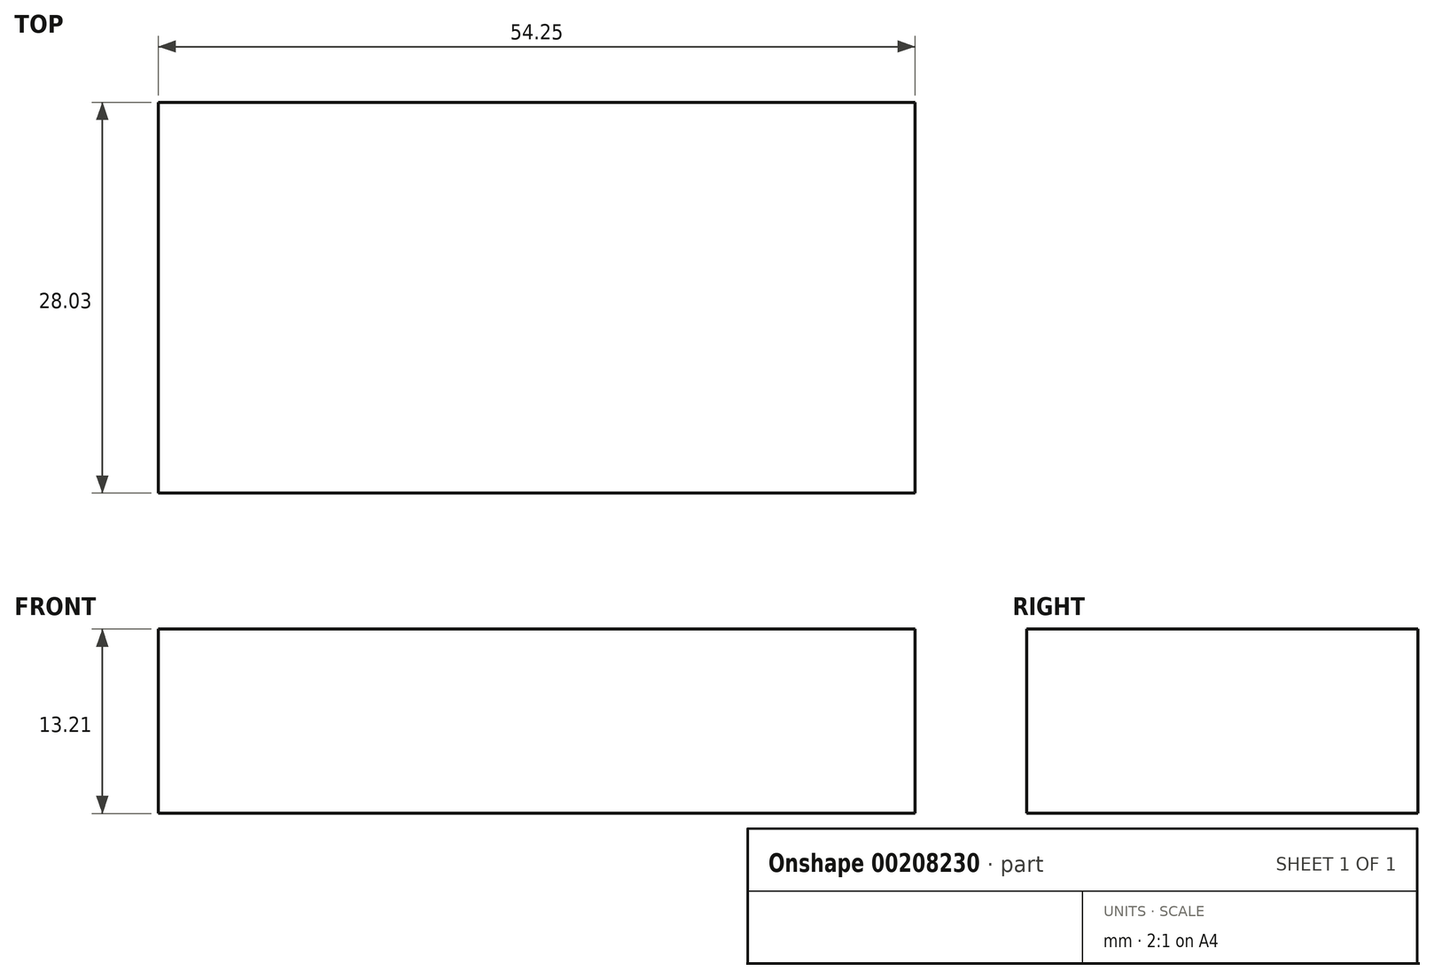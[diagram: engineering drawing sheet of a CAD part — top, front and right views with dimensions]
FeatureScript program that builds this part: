
annotation { "Feature Type Name" : "Feature", "Feature Type Description" : "" }
export const myFeature = defineFeature(function(context is Context, id is Id, definition is map)
    precondition{}
    {
        {
            var Q0;
            Q0=qCreatedBy(makeId("Top.planeOp"),FACE);
            var sketch = newSketch(context, id + "F0", { "sketchPlane" : qUnion([Q0])});
            skLineSegment(sketch, "E0.bottom", {"start": v(-25.4, 14.92) * mm, "end": v(28.85, 14.92) * mm});
            skLineSegment(sketch, "E0.top", {"start": v(-25.4, -13.1) * mm, "end": v(28.85, -13.1) * mm});
            skLineSegment(sketch, "E0.left", {"start": v(-25.4, 14.92) * mm, "end": v(-25.4, -13.1) * mm});
            skLineSegment(sketch, "E0.right", {"start": v(28.85, 14.92) * mm, "end": v(28.85, -13.1) * mm});
            skSolve(sketch);
        }
        {
            var Q0;
            Q0=qCreatedBy(makeId("Front.planeOp"),FACE);
            var sketch = newSketch(context, id + "F1", { "sketchPlane" : qUnion([Q0])});
            skLineSegment(sketch, "E1.bottom", {"start": v(-26, -13.41) * mm, "end": v(29.45, -13.41) * mm});
            skLineSegment(sketch, "E1.top", {"start": v(-26, 14.62) * mm, "end": v(29.45, 14.62) * mm});
            skLineSegment(sketch, "E1.left", {"start": v(-26, -13.41) * mm, "end": v(-26, 14.62) * mm});
            skLineSegment(sketch, "E1.right", {"start": v(29.45, -13.41) * mm, "end": v(29.45, 14.62) * mm});
            skSolve(sketch);
        }
        {
            var Q0;
            Q0=makeQuery(id+"F0.imprint","IMPRINT",FACE,{"disambiguationData":[TD([[makeQuery(id+"F0.imprint","IMPRINT",EDGE,{"derivedFrom":sQuery(id+"F0.wireOp",EDGE,"E0.bottom")}),-1.0]])]});
            extrude(context, id + "F2", {"entities" : qUnion([Q0]), "oppositeDirection" : true, "depth" : 13.2 * mm});
        }
    });
